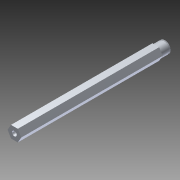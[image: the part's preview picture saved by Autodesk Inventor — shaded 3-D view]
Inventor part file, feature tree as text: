
AUTODESK INVENTOR PART (.ipt)
format: ipt  version: 2015 SP1 (Build 190203100, 203)  size: 120,832 bytes
history: native  units: in
note: dims shown in document units (in); Inventor stores cm internally (conversion verified against a paired STEP export)
features: other x2, extrude x1, imported_body x1, sketch x1, projected_geometry x1
ambient origin geometry x8: Origin, YZ Plane, XZ Plane, XY Plane, X Axis, Y Axis, Z Axis, Center Point
bodies: Body1 (feature_tree)
feature tree (6):
  other  "1_4-20 Tapped Hole1"
  other  "217-3421-004 Rev1.ipt1"
  extrude  "Extrusion1"  Depth=0.5in TaperAngle=0.0deg
  imported_body  "Base1"
  sketch  "Sketch1"  dims[d0=0.6in d1=0.5in d2=0.0in]
  projected_geometry  "Projected Loop1"
